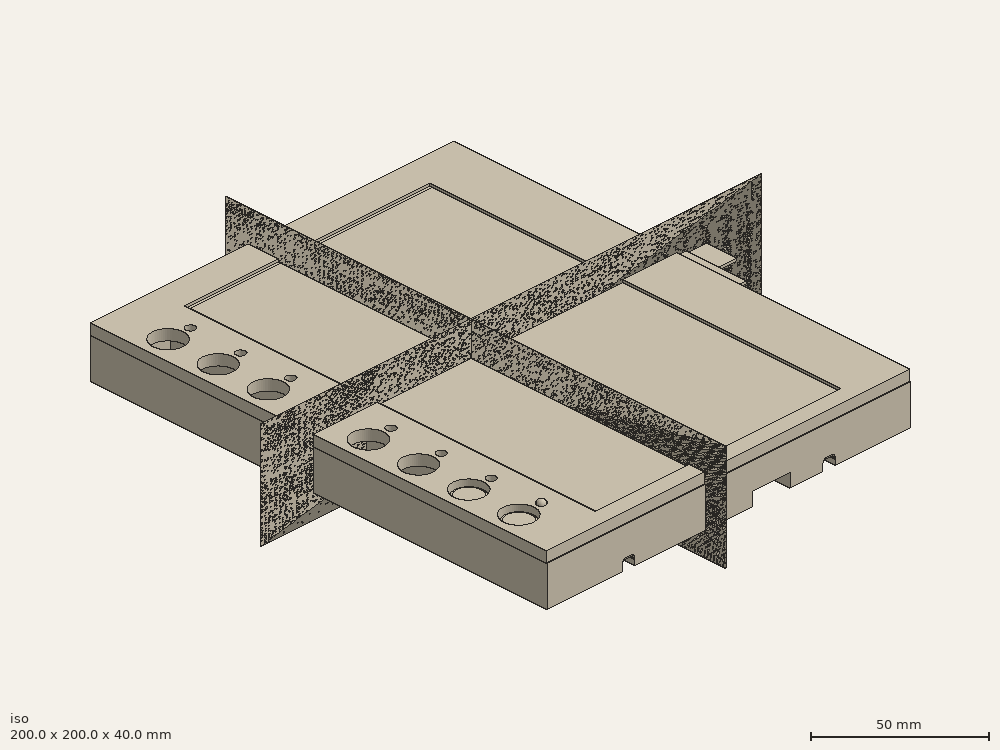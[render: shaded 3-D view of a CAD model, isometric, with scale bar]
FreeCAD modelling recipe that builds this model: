
FCSTD DOCUMENT  (FreeCAD 0.19R)
Label: eInkCase
License: All rights reserved
LicenseURL: http://en.wikipedia.org/wiki/All_rights_reserved
objects: PartDesign::LinearPattern×10, PartDesign::SubtractiveBox×8, PartDesign::AdditiveBox×7, PartDesign::SubtractiveCylinder×6, PartDesign::MultiTransform×4, PartDesign::Body×3, Part::Feature×3, Part::Box×2, PartDesign::Fillet×2
note: 68 computed .brp shape members not serialized (recipe doc carries the construction recipe); baked Part::Feature solids carry a one-line shape summary decoded from their .brp

FEATURE [Part::Box] Box003  label="V_Slice"
  AttacherType = Attacher::AttachEngine3D
  Height = 40
  Length = 1e-05
  Placement = pos=(63,-9,-20) rot=(0,0,1;0rad)
  Width = 200
FEATURE [Part::Box] Box004  label="H_Slice"
  AttacherType = Attacher::AttachEngine3D
  Height = 40
  Length = 200
  Placement = pos=(-21,93,-20) rot=(0,0,1;0rad)
  Width = 1e-06
FEATURE [PartDesign::AdditiveBox] Box005  label="BottomBody"
  AttacherType = Attacher::AttachEngine3D
  AttachmentOffset = pos=(0,-11,-182) rot=(0,0,1;0rad)
  Height = 182.3
  Length = 145
  MapMode = 5
  Placement = pos=(0,182,-11) rot=(1,0,0;1.5708rad)
  Support = -> [XZ_Plane001]
  Width = 15
FEATURE [PartDesign::SubtractiveBox] Box006  label="ButtonSpace"
  AttacherType = Attacher::AttachEngine3D
  AttachmentOffset = pos=(2,8,-9) rot=(0,0,1;0rad)
  BaseFeature = -> Box005
  Height = 13
  Length = 19
  MapMode = 5
  Placement = pos=(2,8,-9) rot=(0,0,1;0rad)
  Support = -> [XY_Plane001]
  Width = 163
FEATURE [PartDesign::SubtractiveBox] Box007  label="ScreenSpace"
  AttacherType = Attacher::AttachEngine3D
  AttachmentOffset = pos=(23,2,2.5) rot=(0,0,1;0rad)
  BaseFeature = -> Box006
  Height = 1.5
  Length = 112
  MapMode = 5
  Placement = pos=(23,2,2.5) rot=(0,0,1;0rad)
  Support = -> [XY_Plane001]
  Width = 172
FEATURE [PartDesign::AdditiveBox] Box  label="Case"
  AttacherType = Attacher::AttachEngine3D
  Height = 4
  Length = 145
  Width = 182
FEATURE [PartDesign::SubtractiveBox] Box001  label="ScreenDivot"
  AttacherType = Attacher::AttachEngine3D
  AttachmentOffset = pos=(25.5,6,-5) rot=(0,0,1;0rad)
  BaseFeature = -> Box
  Height = 5
  Length = 98
  MapMode = 5
  Placement = pos=(25.5,6,-1) rot=(0,0,1;0rad)
  Support = -> [Box]
  Width = 164
FEATURE [PartDesign::SubtractiveCylinder] Cylinder  label="ButtonHole"
  Angle = 360
  AttacherType = Attacher::AttachEngine3D
  AttachmentOffset = pos=(9,20,-11) rot=(0,0,1;0rad)
  BaseFeature = -> Box001
  Height = 12
  MapMode = 5
  Placement = pos=(9,20,-7) rot=(0,0,1;0rad)
  Radius = 6
  Support = -> [Box]
FEATURE [PartDesign::SubtractiveCylinder] Cylinder001  label="LedHole"
  Angle = 360
  AttacherType = Attacher::AttachEngine3D
  AttachmentOffset = pos=(18,20,-11) rot=(0,0,1;0rad)
  BaseFeature = -> Cylinder
  Height = 12
  MapMode = 5
  Placement = pos=(18,20,-7) rot=(0,0,1;0rad)
  Radius = 1.75
  Support = -> [Box]
FEATURE [PartDesign::LinearPattern] LinearPattern  label="ButtonRepeat"
  BaseFeature = -> Cylinder001
  Direction = -> Y_Axis
  Length = 140
  Occurrences = 8
  Originals = -> [Cylinder,Cylinder001]
  Placement = pos=(18,20,-7) rot=(0,0,1;0rad)
FEATURE [PartDesign::SubtractiveBox] Box008  label="ScreenCableSpace"
  AttacherType = Attacher::AttachEngine3D
  AttachmentOffset = pos=(134,69,2) rot=(0,0,1;0rad)
  BaseFeature = -> Box007
  Height = 2
  Length = 11
  MapMode = 5
  Placement = pos=(134,69,2) rot=(0,0,1;0rad)
  Support = -> [XY_Plane001]
  Width = 32
FEATURE [PartDesign::SubtractiveBox] Box009  label="CableSpace"
  AttacherType = Attacher::AttachEngine3D
  AttachmentOffset = pos=(142,79,-12) rot=(0,0,1;0rad)
  BaseFeature = -> Box008
  Height = 17
  Length = 3
  MapMode = 5
  Placement = pos=(142,79,-12) rot=(0,0,1;0rad)
  Support = -> [XY_Plane001]
  Width = 24
FEATURE [PartDesign::SubtractiveBox] Box010  label="BoardSpace"
  AttacherType = Attacher::AttachEngine3D
  AttachmentOffset = pos=(82,75,-11) rot=(0,0,1;0rad)
  BaseFeature = -> Box009
  Height = 5
  Length = 60
  MapMode = 5
  Placement = pos=(82,75,-11) rot=(0,0,1;0rad)
  Support = -> [XY_Plane001]
  Width = 32
FEATURE [PartDesign::SubtractiveBox] Box011  label="LongCableSpace"
  AttacherType = Attacher::AttachEngine3D
  AttachmentOffset = pos=(82,-2,-11) rot=(0,0,1;0rad)
  BaseFeature = -> Box010
  Height = 5
  Length = 15
  MapMode = 5
  Placement = pos=(82,-2,-11) rot=(0,0,1;0rad)
  Support = -> [XY_Plane001]
  Width = 80
FEATURE [PartDesign::SubtractiveBox] Box012  label="LegSpace"
  AttacherType = Attacher::AttachEngine3D
  AttachmentOffset = pos=(30,-1,-11) rot=(0,0,1;0rad)
  BaseFeature = -> Box011
  Height = 3
  Length = 5
  MapMode = 5
  Placement = pos=(30,-1,-11) rot=(0,0,1;0rad)
  Support = -> [XY_Plane001]
  Width = 70
FEATURE [PartDesign::LinearPattern] LinearPattern001  label="LegSpacePattern"
  BaseFeature = -> Box012
  Direction = -> X_Axis001
  Length = 80
  Occurrences = 2
  Originals = -> [Box012]
  Placement = pos=(30,-1,-11) rot=(0,0,1;0rad)
FEATURE [PartDesign::Fillet] Fillet  label="LegFiller"
  Base = -> LinearPattern001 [Face23]
  BaseFeature = -> LinearPattern001
  Placement = pos=(30,-1,-11) rot=(0,0,1;0rad)
  Radius = 1
  SupportTransform = false
FEATURE [PartDesign::Fillet] Fillet001  label="LegPatternFillet"
  Base = -> Fillet [Face15]
  BaseFeature = -> Fillet
  Placement = pos=(30,-1,-11) rot=(0,0,1;0rad)
  Radius = 1
  SupportTransform = false
FEATURE [PartDesign::SubtractiveCylinder] Cylinder002  label="ScrewHole"
  Angle = 360
  AttacherType = Attacher::AttachEngine3D
  AttachmentOffset = pos=(5,5,-13) rot=(0,0,1;0rad)
  BaseFeature = -> Fillet001
  Height = 20
  MapMode = 5
  Placement = pos=(5,5,-13) rot=(0,0,1;0rad)
  Radius = 1
  Support = -> [XY_Plane001]
FEATURE [PartDesign::LinearPattern] LinearPattern002
  Direction = -> X_Axis001
  Length = 133
  Occurrences = 2
  Placement = pos=(5,5,-13) rot=(0,0,1;0rad)
FEATURE [PartDesign::LinearPattern] LinearPattern003
  Direction = -> Y_Axis001
  Length = 170
  Occurrences = 2
  Placement = pos=(5,5,-13) rot=(0,0,1;0rad)
FEATURE [PartDesign::MultiTransform] MultiTransform
  BaseFeature = -> Cylinder002
  Originals = -> [Cylinder002]
  Placement = pos=(5,5,-13) rot=(0,0,1;0rad)
  Transformations = -> [LinearPattern002,LinearPattern003]
FEATURE [PartDesign::SubtractiveCylinder] Cylinder003  label="ScrewHole001"
  Angle = 360
  AttacherType = Attacher::AttachEngine3D
  AttachmentOffset = pos=(5,5,-3) rot=(0,0,1;0rad)
  BaseFeature = -> LinearPattern
  Height = 6
  MapMode = 5
  Placement = pos=(5,5,-3) rot=(0,0,1;0rad)
  Radius = 1
  Support = -> [XY_Plane001]
FEATURE [PartDesign::LinearPattern] LinearPattern004
  Direction = -> X_Axis
  Length = 133
  Occurrences = 2
  Placement = pos=(5,5,-3) rot=(0,0,1;0rad)
FEATURE [PartDesign::LinearPattern] LinearPattern005
  Direction = -> Y_Axis
  Length = 170
  Occurrences = 2
  Placement = pos=(5,5,-3) rot=(0,0,1;0rad)
FEATURE [PartDesign::MultiTransform] MultiTransform001
  BaseFeature = -> Cylinder003
  Originals = -> [Cylinder003]
  Placement = pos=(5,5,-3) rot=(0,0,1;0rad)
  Transformations = -> [LinearPattern004,LinearPattern005]
FEATURE [PartDesign::Body] Body
  Group = -> [Box,Box001,Cylinder,Cylinder001,LinearPattern,Cylinder003,MultiTransform001,LinearPattern004,LinearPattern005]
  Origin = -> Origin
  Placement = pos=(0,0,4) rot=(0,0,1;0rad)
  Tip = -> MultiTransform001
FEATURE [Part::Feature] Feature  label="12mmx12mm With Black cap round"
  Placement = pos=(9.125,20,-4) rot=(0,0,1;0rad)
  shape: bbox 14.09 x 14.09 x 13.07 mm, 321 faces, 2 solids (baked)
FEATURE [Part::Feature] Feature002  label="LED 3mm Red 6mm Leads"
  Placement = pos=(18,20,1) rot=(0,0,1;0rad)
  shape: bbox 3.534 x 3.928 x 11.38 mm, 57 faces, 3 solids (baked)
FEATURE [PartDesign::AdditiveBox] Box013  label="ButtonShelf"
  AttacherType = Attacher::AttachEngine3D
  AttachmentOffset = pos=(4,8,-9) rot=(0,0,1;0rad)
  BaseFeature = -> MultiTransform
  Height = 4
  Length = 11
  MapMode = 5
  Placement = pos=(4,8,-9) rot=(0,0,1;0rad)
  Support = -> [XY_Plane001]
  Width = 165
FEATURE [PartDesign::SubtractiveCylinder] Cylinder004  label="ButtonGuideHole"
  Angle = 360
  AttacherType = Attacher::AttachEngine3D
  AttachmentOffset = pos=(9.125,15.625,-8) rot=(0,0,1;0rad)
  BaseFeature = -> Box013
  Height = 3
  MapMode = 5
  Placement = pos=(9.125,15.625,-8) rot=(0,0,1;0rad)
  Radius = 1
  Support = -> [XY_Plane001]
FEATURE [PartDesign::LinearPattern] LinearPattern006
  Direction = -> Y_Axis001
  Length = 9
  Occurrences = 2
  Placement = pos=(9.125,15.625,-8) rot=(0,0,1;0rad)
FEATURE [PartDesign::LinearPattern] LinearPattern007
  Direction = -> Y_Axis001
  Length = 140
  Occurrences = 8
  Placement = pos=(9.125,15.625,-8) rot=(0,0,1;0rad)
FEATURE [PartDesign::MultiTransform] MultiTransform002  label="ButtonGuideTransform"
  BaseFeature = -> Cylinder004
  Originals = -> [Cylinder004]
  Placement = pos=(9.125,15.625,-8) rot=(0,0,1;0rad)
  Transformations = -> [LinearPattern006,LinearPattern007]
FEATURE [Part::Feature] Feature003  label="12mmx12mm With Black cap round001"
  Placement = pos=(9.125,40,-4) rot=(0,0,1;0rad)
  shape: bbox 14.09 x 14.09 x 13.07 mm, 321 faces, 2 solids (baked)
FEATURE [PartDesign::SubtractiveCylinder] Cylinder005  label="ScrewAccessHole"
  Angle = 360
  AttacherType = Attacher::AttachEngine3D
  AttachmentOffset = pos=(5,5,-12) rot=(0,0,1;0rad)
  BaseFeature = -> MultiTransform002
  Height = 10
  MapMode = 5
  Placement = pos=(5,5,-12) rot=(0,0,1;0rad)
  Radius = 3
  Support = -> [XY_Plane001]
FEATURE [PartDesign::LinearPattern] LinearPattern008
  Direction = -> X_Axis001
  Length = 133
  Occurrences = 2
  Placement = pos=(5,5,-12) rot=(0,0,1;0rad)
FEATURE [PartDesign::LinearPattern] LinearPattern009
  Direction = -> Y_Axis001
  Length = 170
  Occurrences = 2
  Placement = pos=(5,5,-12) rot=(0,0,1;0rad)
FEATURE [PartDesign::MultiTransform] MultiTransform003
  BaseFeature = -> Cylinder005
  Originals = -> [Cylinder005]
  Placement = pos=(5,5,-12) rot=(0,0,1;0rad)
  Transformations = -> [LinearPattern008,LinearPattern009]
FEATURE [PartDesign::Body] Body001  label="BottomCase"
  Group = -> [Box005,Box006,Box007,Box008,Box009,Box010,Box011,Box012,LinearPattern001,Fillet,Fillet001,Cylinder002,MultiTransform,LinearPattern002,LinearPattern003,Box013,Cylinder004,MultiTransform002,LinearPattern006,LinearPattern007,Cylinder005,MultiTransform003,LinearPattern008,LinearPattern009]
  Origin = -> Origin001
  Tip = -> MultiTransform003
FEATURE [PartDesign::AdditiveBox] Box014  label="Screen"
  AttacherType = Attacher::AttachEngine3D
  Height = 1
  Length = 111
  MapMode = 5
  Support = -> [XY_Plane002]
  Width = 170
FEATURE [PartDesign::AdditiveBox] Box015  label="Cable"
  AttacherType = Attacher::AttachEngine3D
  AttachmentOffset = pos=(111,66,0) rot=(0,0,1;0rad)
  BaseFeature = -> Box014
  Height = 1
  Length = 14
  MapMode = 5
  Placement = pos=(111,66,0) rot=(0,0,1;0rad)
  Support = -> [XY_Plane002]
  Width = 31
FEATURE [PartDesign::AdditiveBox] Box016  label="CableTail"
  AttacherType = Attacher::AttachEngine3D
  AttachmentOffset = pos=(125,77,0) rot=(0,0,1;0rad)
  BaseFeature = -> Box015
  Height = 1
  Length = 7
  MapMode = 5
  Placement = pos=(125,77,0) rot=(0,0,1;0rad)
  Support = -> [XY_Plane002]
  Width = 12
FEATURE [PartDesign::AdditiveBox] Box017
  AttacherType = Attacher::AttachEngine3D
  AttachmentOffset = pos=(3,3,0) rot=(0,0,1;0rad)
  BaseFeature = -> Box016
  Height = 1
  Length = 97
  MapMode = 5
  Placement = pos=(3,3,0) rot=(0,0,1;0rad)
  Support = -> [XY_Plane002]
  Width = 163
FEATURE [PartDesign::Body] Body002  label="Waveshare Board"
  Group = -> [Box014,Box015,Box016,Box017]
  Origin = -> Origin002
  Placement = pos=(24,3,6) rot=(0,0,1;0rad)
  Tip = -> Box017
